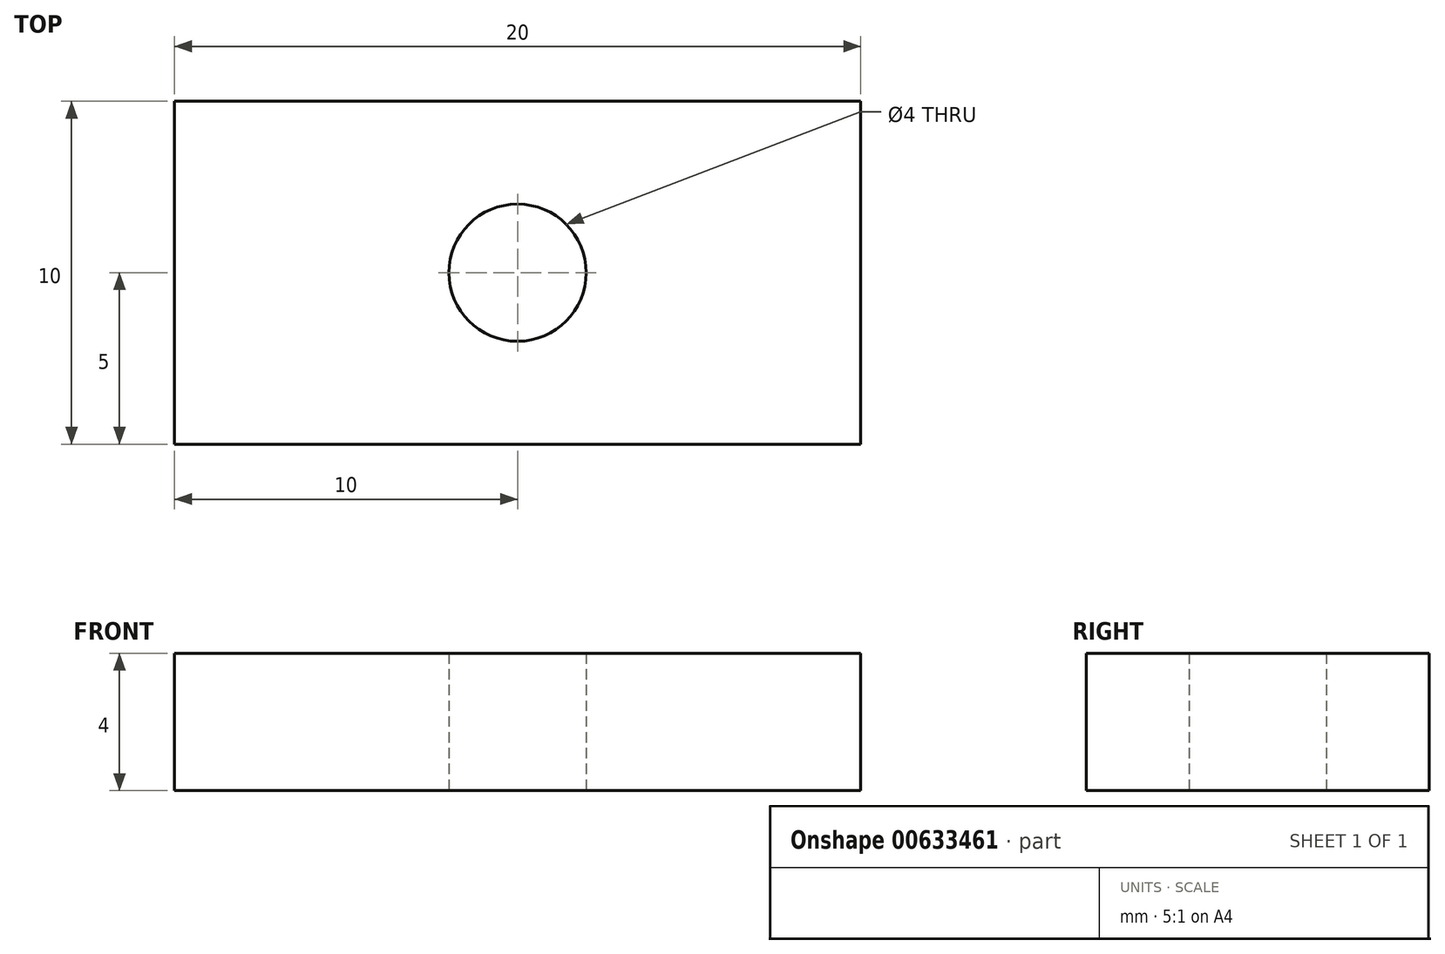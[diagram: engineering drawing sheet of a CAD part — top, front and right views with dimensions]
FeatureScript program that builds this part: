
annotation { "Feature Type Name" : "Feature", "Feature Type Description" : "" }
export const myFeature = defineFeature(function(context is Context, id is Id, definition is map)
    precondition{}
    {
        {
            var Q0;
            Q0=qCreatedBy(makeId("Top.planeOp"),FACE);
            var sketch = newSketch(context, id + "F0", { "sketchPlane" : qUnion([Q0])});
            skLineSegment(sketch, "E0.bottom", {"start": v(0, 0) * mm, "end": v(-20, 0) * mm});
            skLineSegment(sketch, "E0.top", {"start": v(0, 10) * mm, "end": v(-20, 10) * mm});
            skLineSegment(sketch, "E0.left", {"start": v(0, 0) * mm, "end": v(0, 10) * mm});
            skLineSegment(sketch, "E0.right", {"start": v(-20, 0) * mm, "end": v(-20, 10) * mm});
            skLineSegment(sketch, "E1.bottom", {"start": v(-2.5, 10) * mm, "end": v(-17.5, 10) * mm});
            skLineSegment(sketch, "E1.top", {"start": v(-2.5, 14) * mm, "end": v(-17.5, 14) * mm});
            skLineSegment(sketch, "E1.left", {"start": v(-2.5, 10) * mm, "end": v(-2.5, 14) * mm});
            skLineSegment(sketch, "E1.right", {"start": v(-17.5, 10) * mm, "end": v(-17.5, 14) * mm});
            skCircle(sketch, "E2", {"center": v(-10, 5) * mm, "radius": 2 * mm});
            skSolve(sketch);
        }
        {
            var Q0;
            Q0=makeQuery(id+"F0.imprint","IMPRINT",FACE,{"disambiguationData":[TD([[makeQuery(id+"F0.imprint","IMPRINT",EDGE,{"derivedFrom":sQuery(id+"F0.wireOp",EDGE,"E0.bottom")}),-1.0]])]});
            var Q1;
            Q1=makeQuery(id+"F0.imprint","IMPRINT",FACE,{"disambiguationData":[TD([[makeQuery(id+"F0.imprint","IMPRINT",EDGE,{"derivedFrom":sQuery(id+"F0.wireOp",EDGE,"E1.bottom")}),-1.0]])]});
            extrude(context, id + "F1", {"entities" : qUnion([Q0, Q1]), "depth" : 4 * mm, "offsetDistance" : 25 * mm});
        }
    });
